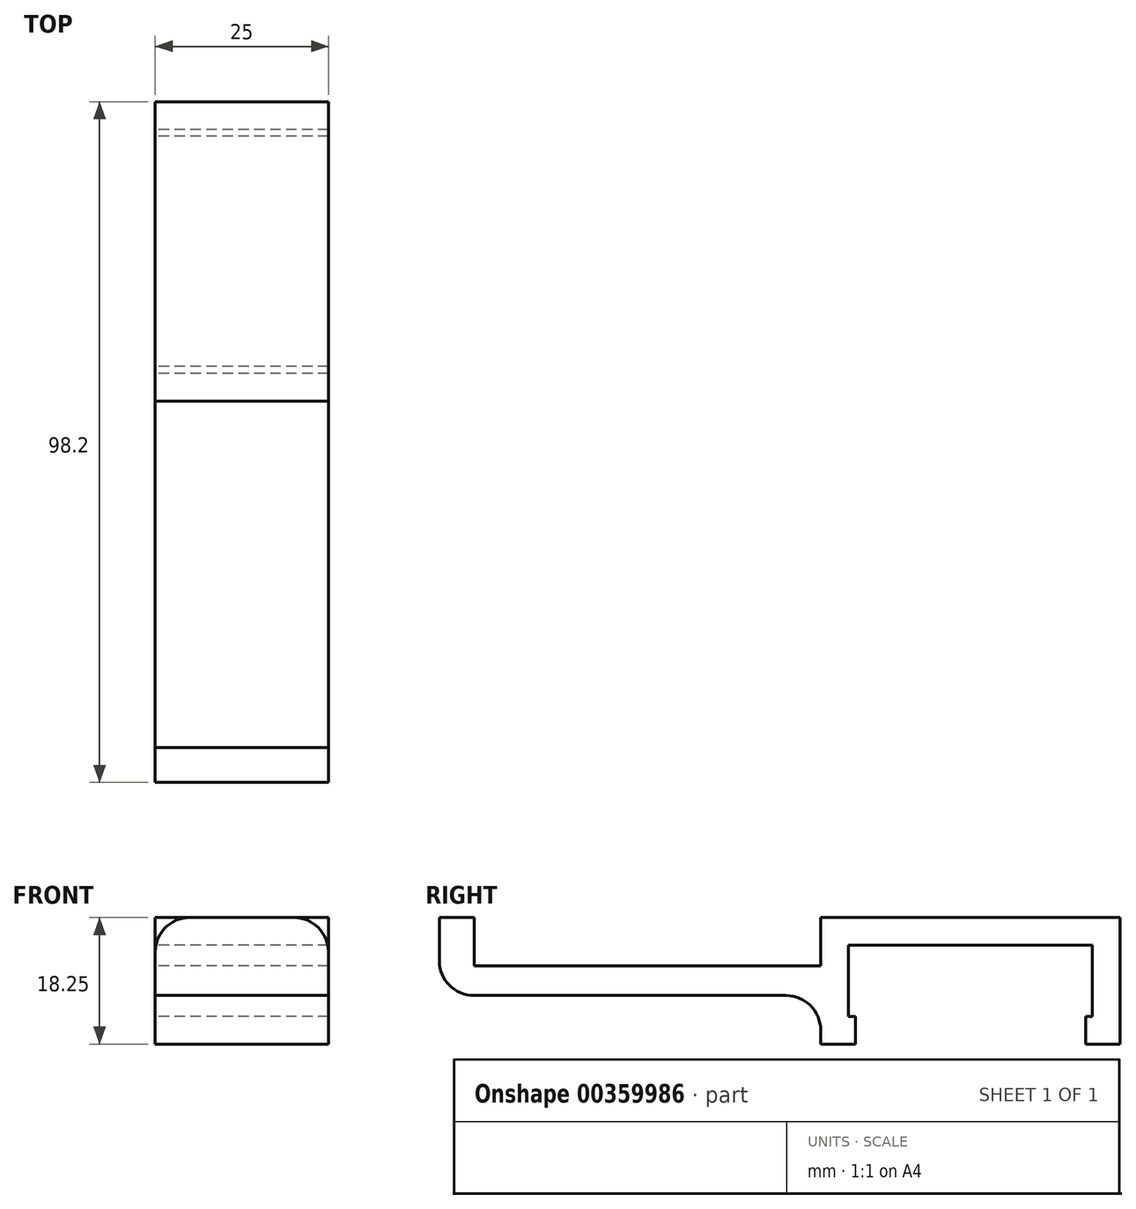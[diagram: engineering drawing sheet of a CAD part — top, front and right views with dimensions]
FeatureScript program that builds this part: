
annotation { "Feature Type Name" : "Feature", "Feature Type Description" : "" }
export const myFeature = defineFeature(function(context is Context, id is Id, definition is map)
    precondition{}
    {
        {
            var Q0;
            Q0=qCreatedBy(makeId("Right.planeOp"),FACE);
            var sketch = newSketch(context, id + "F0", { "sketchPlane" : qUnion([Q0])});
            skLineSegment(sketch, "E0", {"start": v(0, 0) * mm, "end": v(17.5, 0) * mm});
            skLineSegment(sketch, "E1", {"start": v(17.5, 0) * mm, "end": v(17.5, -10.05) * mm});
            skLineSegment(sketch, "E2", {"start": v(17.5, -10.05) * mm, "end": v(14.2, -10.05) * mm});
            skLineSegment(sketch, "E3", {"start": v(14.2, -10.05) * mm, "end": v(14.2, -6.25) * mm});
            skLineSegment(sketch, "E4", {"start": v(14.2, -6.25) * mm, "end": v(8.2, -6.25) * mm});
            skLineSegment(sketch, "E5", {"start": v(8.2, -6.25) * mm, "end": v(8.2, -27.41) * mm});
            skLineSegment(sketch, "E6", {"start": v(8.2, -27.41) * mm, "end": v(-8.2, -27.41) * mm});
            skLineSegment(sketch, "E7", {"start": v(-8.2, -27.41) * mm, "end": v(-8.2, -6.25) * mm});
            skLineSegment(sketch, "E8", {"start": v(-8.2, -6.25) * mm, "end": v(-14.2, -6.25) * mm});
            skLineSegment(sketch, "E9", {"start": v(-14.2, -6.25) * mm, "end": v(-14.2, -10.05) * mm});
            skLineSegment(sketch, "E10", {"start": v(-14.2, -10.05) * mm, "end": v(-17.5, -10.05) * mm});
            skLineSegment(sketch, "E11", {"start": v(-17.5, -10.05) * mm, "end": v(-17.5, 0) * mm});
            skLineSegment(sketch, "E12", {"start": v(-17.5, 0) * mm, "end": v(0, 0) * mm});
            skLineSegment(sketch, "E13.0", {"start": v(17.6, -10.15) * mm, "end": v(16.6, -10.15) * mm});
            skLineSegment(sketch, "E13.1", {"start": v(17.6, 0.1) * mm, "end": v(17.6, -10.15) * mm});
            skLineSegment(sketch, "E13.2", {"start": v(-16.6, -10.15) * mm, "end": v(-17.6, -10.15) * mm});
            skLineSegment(sketch, "E13.3", {"start": v(-17.6, -10.15) * mm, "end": v(-17.6, 0.1) * mm});
            skLineSegment(sketch, "E13.4", {"start": v(-17.6, 0.1) * mm, "end": v(0, 0.1) * mm});
            skLineSegment(sketch, "E13.5", {"start": v(0, 0.1) * mm, "end": v(17.6, 0.1) * mm});
            skLineSegment(sketch, "E14.0", {"start": v(21.6, -14.15) * mm, "end": v(16.6, -14.15) * mm});
            skLineSegment(sketch, "E14.1", {"start": v(21.6, 4.1) * mm, "end": v(21.6, -14.15) * mm});
            skLineSegment(sketch, "E14.2", {"start": v(-16.6, -14.15) * mm, "end": v(-21.6, -14.15) * mm});
            skLineSegment(sketch, "E14.3", {"start": v(-21.6, -14.15) * mm, "end": v(-21.6, 4.1) * mm});
            skLineSegment(sketch, "E14.4", {"start": v(-21.6, 4.1) * mm, "end": v(0, 4.1) * mm});
            skLineSegment(sketch, "E14.5", {"start": v(0, 4.1) * mm, "end": v(21.6, 4.1) * mm});
            skLineSegment(sketch, "E15", {"start": v(-16.6, -10.15) * mm, "end": v(-16.6, -14.15) * mm});
            skLineSegment(sketch, "E16", {"start": v(16.6, -10.15) * mm, "end": v(16.6, -14.15) * mm});
            skSolve(sketch);
        }
        {
            var Q0;
            Q0=makeQuery(id+"F0.imprint","IMPRINT",FACE,{"disambiguationData":[TD([[makeQuery(id+"F0.imprint","IMPRINT",EDGE,{"derivedFrom":sQuery(id+"F0.wireOp",EDGE,"E13.0")}),1.0]])]});
            extrude(context, id + "F1", {"entities" : qUnion([Q0]), "depth" : 25 * mm});
        }
        {
            var Q0;
            {var subQ0=sQuery(id+"F0.wireOp",EDGE,"M60YkKbe-sy4h-C4Ip-92it-TQ4iPFRVJRJv");var subQ1=sQuery(id+"F0.wireOp",EDGE,"E14.3");var subQ2=makeQuery(id+"F0.imprint","INTERSECT",VERTEX,{"disambiguationData":[OD(1.0)],"derivedFrom":[subQ1,subQ0]});Q0=makeQuery(id+"F0.imprint","IMPRINT",FACE,{"disambiguationData":[TD([[makeQuery(id+"F0.imprint","IMPRINT",EDGE,{"disambiguationData":[TD([[subQ2,1.0]])],"derivedFrom":subQ1}),1.0]])]});}
            var Q1;
            {var subQ0=sQuery(id+"F0.wireOp",EDGE,"M60YkKbe-sy4h-C4Ip-92it-TQ4iPFRVJRJv");var subQ1=sQuery(id+"F0.wireOp",EDGE,"E14.3");var subQ2=makeQuery(id+"F0.imprint","INTERSECT",VERTEX,{"disambiguationData":[OD(0.0)],"derivedFrom":[subQ1,subQ0]});Q1=makeQuery(id+"F0.imprint","IMPRINT",FACE,{"disambiguationData":[TD([[makeQuery(id+"F0.imprint","IMPRINT",EDGE,{"disambiguationData":[TD([[subQ2,-1.0]])],"derivedFrom":subQ1}),1.0]])]});}
            var Q2;
            {var subQ0=sQuery(id+"F0.wireOp",EDGE,"M60YkKbe-sy4h-C4Ip-92it-TQ4iPFRVJRJv");var subQ1=sQuery(id+"F0.wireOp",EDGE,"E14.3");var subQ2=makeQuery(id+"F0.imprint","INTERSECT",VERTEX,{"disambiguationData":[OD(0.0)],"derivedFrom":[subQ1,subQ0]});Q2=makeQuery(id+"F0.imprint","IMPRINT",FACE,{"disambiguationData":[TD([[makeQuery(id+"F0.imprint","IMPRINT",EDGE,{"disambiguationData":[TD([[subQ2,-1.0]])],"derivedFrom":subQ1}),-1.0]])]});}
            extrude(context, id + "F2", {"entities" : qUnion([Q0, Q1, Q2]), "operationType" : NewBodyOperationType.ADD, "depth" : 25 * mm});
        }
        {
            var Q0;
            Q0=makeQuery(id+"F1.opExtrude","SWEPT_FACE",FACE,{"disambiguationData":[OSD([sQuery(id+"F0.wireOp",EDGE,"E14.3")])]});
            var sketch = newSketch(context, id + "F3", { "sketchPlane" : qUnion([Q0])});
            skLineSegment(sketch, "E17.bottom", {"start": v(25, -2.9) * mm, "end": v(0, -2.9) * mm});
            skLineSegment(sketch, "E17.top", {"start": v(25, -7.15) * mm, "end": v(0, -7.15) * mm});
            skLineSegment(sketch, "E17.left", {"start": v(25, -2.9) * mm, "end": v(25, -7.15) * mm});
            skLineSegment(sketch, "E17.right", {"start": v(0, -2.9) * mm, "end": v(0, -7.15) * mm});
            skSolve(sketch);
        }
        {
            var Q0;
            Q0=makeQuery(id+"F3.imprint","IMPRINT",FACE,{"disambiguationData":[TD([[makeQuery(id+"F3.imprint","IMPRINT",EDGE,{"derivedFrom":sQuery(id+"F3.wireOp",EDGE,"E17.bottom")}),1.0]])]});
            extrude(context, id + "F4", {"entities" : qUnion([Q0]), "operationType" : NewBodyOperationType.ADD, "depth" : 55 * mm});
        }
        {
            var Q0;
            Q0=makeQuery(id+"F4.opExtrude","SWEPT_FACE",FACE,{"disambiguationData":[OSD([sQuery(id+"F3.wireOp",EDGE,"E17.bottom")])]});
            var sketch = newSketch(context, id + "F5", { "sketchPlane" : qUnion([Q0])});
            skLineSegment(sketch, "E18", {"start": v(0, -71.6) * mm, "end": v(25, -71.6) * mm});
            skSolve(sketch);
        }
        {
            var Q0;
            {var subQ0=sQuery(id+"F5.wireOp",EDGE,"E18");Q0=makeQuery(id+"F5.imprint","IMPRINT",FACE,{"disambiguationData":[TD([[makeQuery(id+"F5.imprint","IMPRINT",EDGE,{"derivedFrom":subQ0}),-1.0]])]});}
            var Q1;
            Q1=makeQuery(id+"F1.opExtrude","SWEPT_FACE",FACE,{"disambiguationData":[OSD([sQuery(id+"F0.wireOp",EDGE,"E14.4"),sQuery(id+"F0.wireOp",EDGE,"E14.5")])]});
            extrude(context, id + "F6", {"entities" : qUnion([Q0]), "operationType" : NewBodyOperationType.ADD, "endBound" : BoundingType.UP_TO_SURFACE, "endBoundEntityFace" : qUnion([Q1]), "depth" : 25 * mm, "hasSecondDirectionDraft" : true, "secondDirectionDraftAngle" : 3 * degree, "secondDirectionDraftPullDirection" : true});
        }
        {
            var Q0;
            Q0=makeQuery(id+"F4.opExtrude","CAP_EDGE",EDGE,{"disambiguationData":[OSD([sQuery(id+"F3.wireOp",EDGE,"E17.bottom")])],"isStart":true});
            var Q1;
            Q1=makeQuery(id+"F4.opExtrude","CAP_EDGE",EDGE,{"disambiguationData":[OSD([sQuery(id+"F3.wireOp",EDGE,"E17.top")])],"isStart":true});
            var Q2;
            Q2=makeQuery(id+"F6.opExtrude","CAP_EDGE",EDGE,{"disambiguationData":[OSD([sQuery(id+"F5.wireOp",EDGE,"E18")])],"isStart":true});
            var Q3;
            Q3=makeQuery(id+"F4.opExtrude","CAP_EDGE",EDGE,{"disambiguationData":[OSD([sQuery(id+"F3.wireOp",EDGE,"E17.top")])],"isStart":false});
            fillet(context, id + "F7", {"entities" : qUnion([Q0, Q1, Q2, Q3]), "radius" : 5 * mm, "tangentPropagation" : true, "allowEdgeOverflow" : false});
        }
        {
            var Q0;
            Q0=makeQuery(id+"F6.opExtrude","CAP_EDGE",EDGE,{"disambiguationData":[OSD([sQuery(id+"F0.wireOp",EDGE,"E14.3"),sQuery(id+"F3.wireOp",EDGE,"E17.bottom"),sQuery(id+"F3.wireOp",EDGE,"E17.left")])],"isStart":false});
            var Q1;
            Q1=makeQuery(id+"F6.opExtrude","CAP_EDGE",EDGE,{"disambiguationData":[OSD([sQuery(id+"F0.wireOp",EDGE,"E14.3"),sQuery(id+"F3.wireOp",EDGE,"E17.bottom"),sQuery(id+"F3.wireOp",EDGE,"E17.right")])],"isStart":false});
            fillet(context, id + "F8", {"entities" : qUnion([Q0, Q1]), "radius" : 5 * mm, "tangentPropagation" : true, "allowEdgeOverflow" : false});
        }
    });
